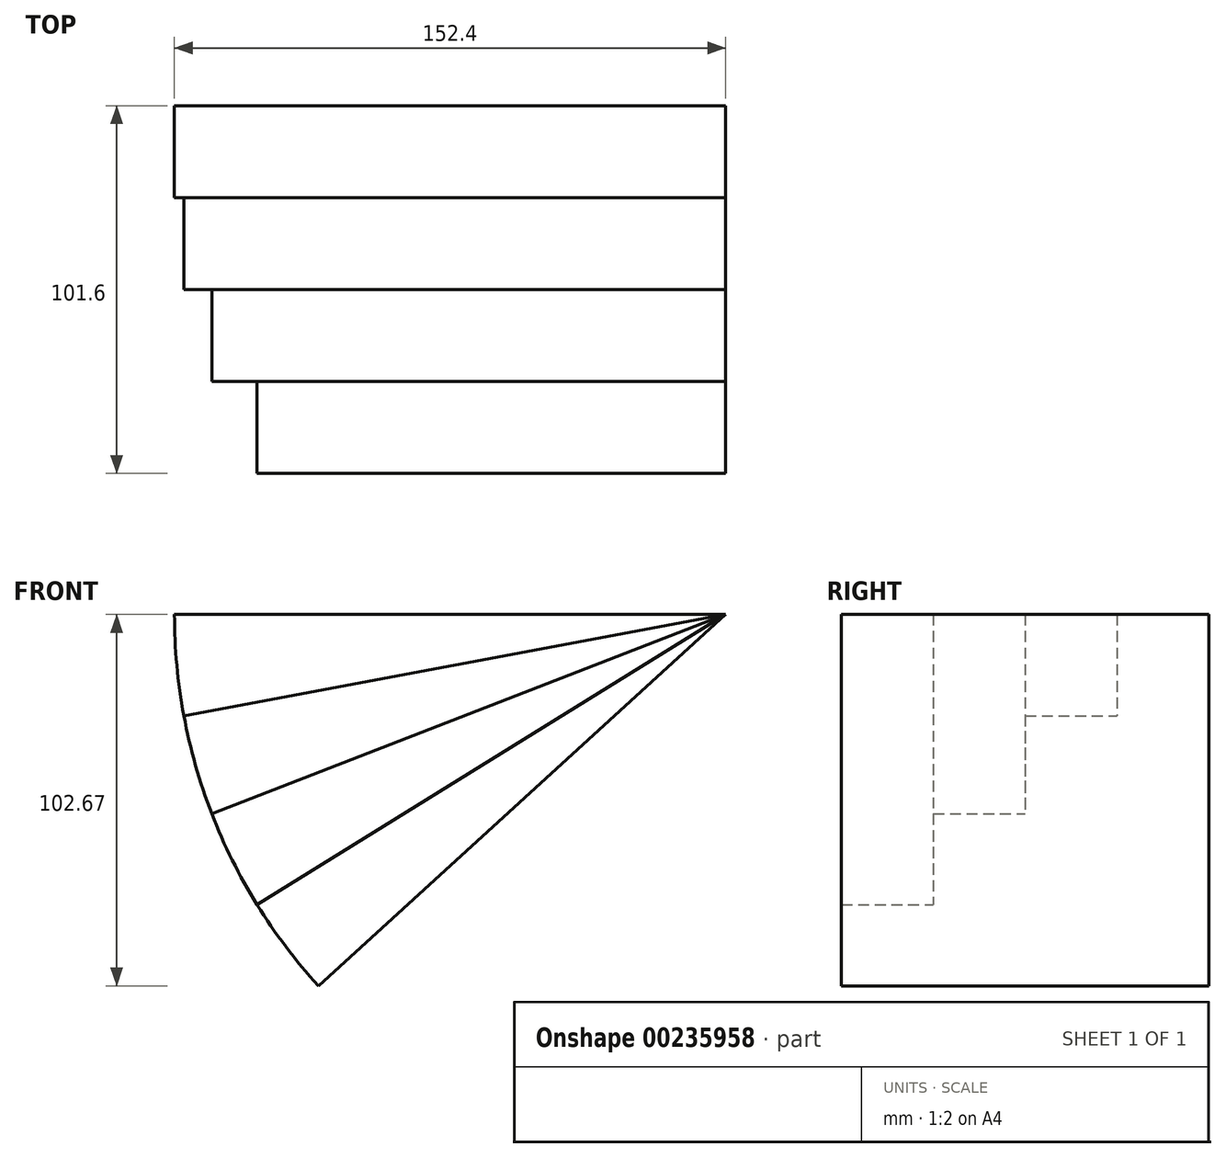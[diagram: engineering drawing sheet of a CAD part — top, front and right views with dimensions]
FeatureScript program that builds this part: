
annotation { "Feature Type Name" : "Feature", "Feature Type Description" : "" }
export const myFeature = defineFeature(function(context is Context, id is Id, definition is map)
    precondition{}
    {
        {
            var Q0;
            Q0=qCreatedBy(makeId("Front.planeOp"),FACE);
            var sketch = newSketch(context, id + "F0", { "sketchPlane" : qUnion([Q0])});
            skCircle(sketch, "E0", {"center": v(0, 0) * mm, "radius": 152.4 * mm});
            skLineSegment(sketch, "E1", {"start": v(0, 0) * mm, "end": v(152.4, 0) * mm});
            skLineSegment(sketch, "E2.1.0", {"start": v(0, 0) * mm, "end": v(149.8, -28) * mm});
            skLineSegment(sketch, "E2.2.0", {"start": v(0, 0) * mm, "end": v(142.1, -55.05) * mm});
            skLineSegment(sketch, "E2.3.0", {"start": v(0, 0) * mm, "end": v(129.57, -80.23) * mm});
            skLineSegment(sketch, "E2.4.0", {"start": v(0, 0) * mm, "end": v(112.62, -102.67) * mm});
            skLineSegment(sketch, "E2.5.0", {"start": v(0, 0) * mm, "end": v(91.84, -121.62) * mm});
            skLineSegment(sketch, "E2.6.0", {"start": v(0, 0) * mm, "end": v(67.93, -136.42) * mm});
            skLineSegment(sketch, "E2.7.0", {"start": v(0, 0) * mm, "end": v(41.7, -146.58) * mm});
            skLineSegment(sketch, "E2.8.0", {"start": v(0, 0) * mm, "end": v(14.06, -151.75) * mm});
            skLineSegment(sketch, "E2.9.0", {"start": v(0, 0) * mm, "end": v(-14.06, -151.75) * mm});
            skLineSegment(sketch, "E2.10.0", {"start": v(0, 0) * mm, "end": v(-41.7, -146.58) * mm});
            skLineSegment(sketch, "E2.11.0", {"start": v(0, 0) * mm, "end": v(-67.93, -136.42) * mm});
            skLineSegment(sketch, "E2.12.0", {"start": v(0, 0) * mm, "end": v(-91.84, -121.62) * mm});
            skLineSegment(sketch, "E2.13.0", {"start": v(0, 0) * mm, "end": v(-112.62, -102.67) * mm});
            skLineSegment(sketch, "E2.14.0", {"start": v(0, 0) * mm, "end": v(-129.57, -80.23) * mm});
            skLineSegment(sketch, "E2.15.0", {"start": v(0, 0) * mm, "end": v(-142.1, -55.05) * mm});
            skLineSegment(sketch, "E2.16.0", {"start": v(0, 0) * mm, "end": v(-149.8, -28) * mm});
            skLineSegment(sketch, "E2.17.0", {"start": v(0, 0) * mm, "end": v(-152.4, 0) * mm});
            skLineSegment(sketch, "E2.anchor1", {"start": v(0, 0) * mm, "end": v(152.4, 0) * mm, "construction": true});
            skLineSegment(sketch, "E2.anchor2", {"start": v(0, 0) * mm, "end": v(-152.4, 0) * mm, "construction": true});
            skSolve(sketch);
        }
        {
            var Q0;
            {var subQ0=sQuery(id+"F0.wireOp",EDGE,"E2.16.0");Q0=makeQuery(id+"F0.imprint","IMPRINT",FACE,{"disambiguationData":[TD([[makeQuery(id+"F0.imprint","IMPRINT",EDGE,{"derivedFrom":subQ0}),-1.0]])]});}
            extrude(context, id + "F1", {"entities" : qUnion([Q0]), "depth" : 25.4 * mm});
        }
        {
            var Q0;
            {var subQ0=sQuery(id+"F0.wireOp",EDGE,"E2.15.0");Q0=makeQuery(id+"F0.imprint","IMPRINT",FACE,{"disambiguationData":[TD([[makeQuery(id+"F0.imprint","IMPRINT",EDGE,{"derivedFrom":subQ0}),-1.0]])]});}
            extrude(context, id + "F2", {"entities" : qUnion([Q0]), "operationType" : NewBodyOperationType.ADD, "depth" : 50.8 * mm});
        }
        {
            var Q0;
            {var subQ0=sQuery(id+"F0.wireOp",EDGE,"E2.14.0");Q0=makeQuery(id+"F0.imprint","IMPRINT",FACE,{"disambiguationData":[TD([[makeQuery(id+"F0.imprint","IMPRINT",EDGE,{"derivedFrom":subQ0}),-1.0]])]});}
            extrude(context, id + "F3", {"entities" : qUnion([Q0]), "operationType" : NewBodyOperationType.ADD, "depth" : 76.2 * mm});
        }
        {
            var Q0;
            {var subQ0=sQuery(id+"F0.wireOp",EDGE,"E2.13.0");Q0=makeQuery(id+"F0.imprint","IMPRINT",FACE,{"disambiguationData":[TD([[makeQuery(id+"F0.imprint","IMPRINT",EDGE,{"derivedFrom":subQ0}),-1.0]])]});}
            extrude(context, id + "F4", {"entities" : qUnion([Q0]), "operationType" : NewBodyOperationType.ADD, "depth" : 101.6 * mm});
        }
    });
